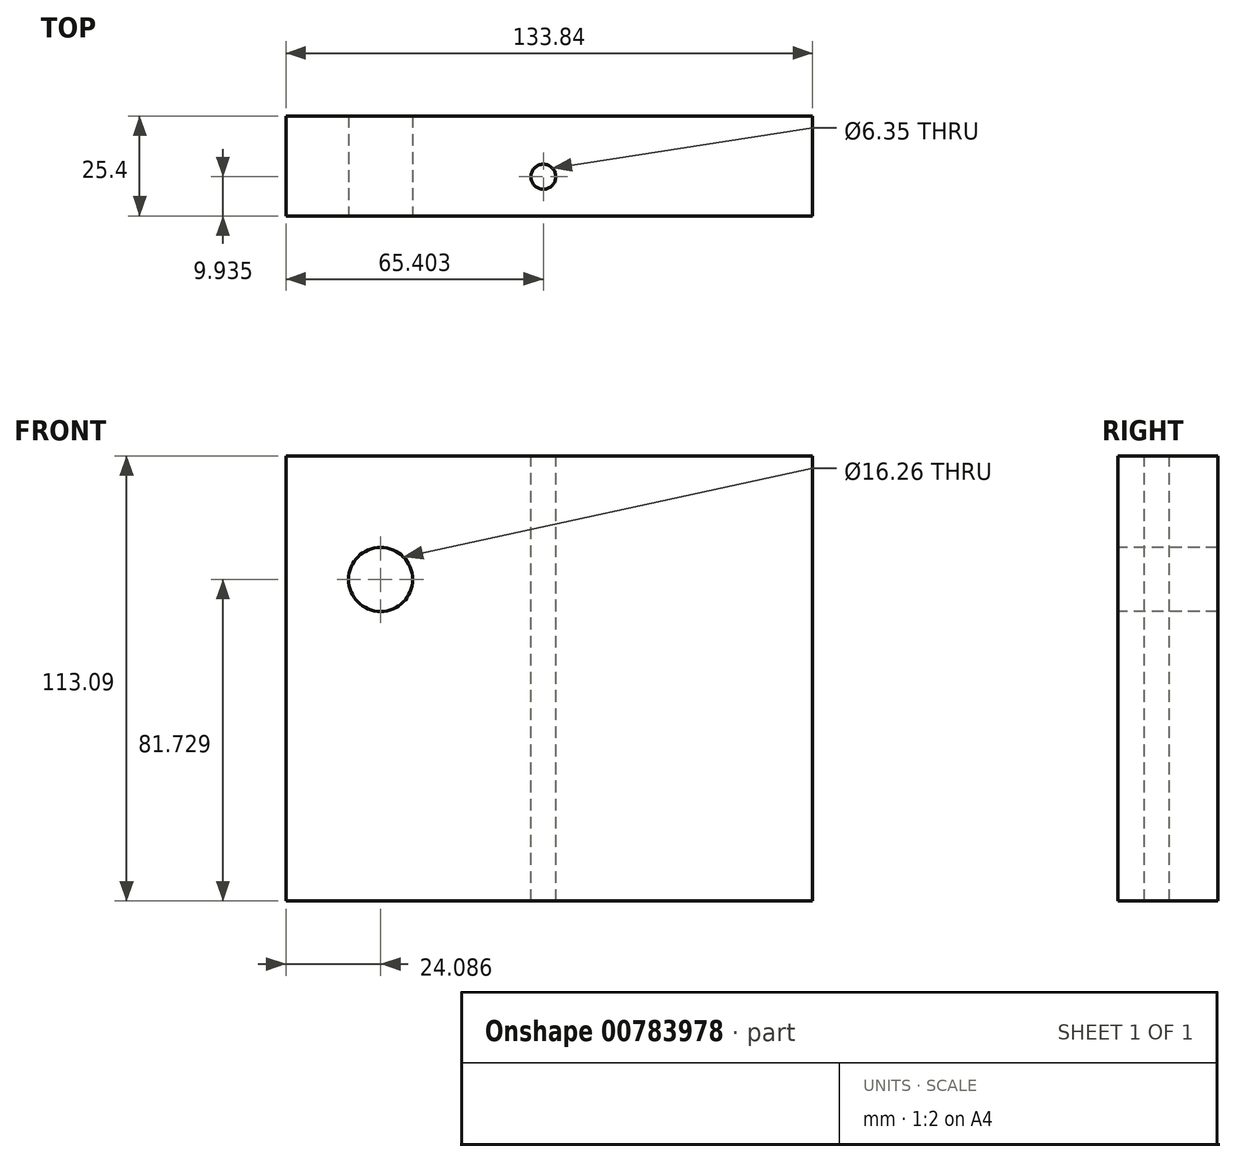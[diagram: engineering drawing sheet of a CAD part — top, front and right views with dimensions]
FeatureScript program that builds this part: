
annotation { "Feature Type Name" : "Feature", "Feature Type Description" : "" }
export const myFeature = defineFeature(function(context is Context, id is Id, definition is map)
    precondition{}
    {
        {
            var Q0;
            Q0=qCreatedBy(makeId("Front.planeOp"),FACE);
            var sketch = newSketch(context, id + "F0", { "sketchPlane" : qUnion([Q0])});
            skLineSegment(sketch, "E0.bottom", {"start": v(0, 0) * mm, "end": v(133.84, 0) * mm});
            skLineSegment(sketch, "E0.top", {"start": v(0, 113.09) * mm, "end": v(133.84, 113.09) * mm});
            skLineSegment(sketch, "E0.left", {"start": v(0, 0) * mm, "end": v(0, 113.09) * mm});
            skLineSegment(sketch, "E0.right", {"start": v(133.84, 0) * mm, "end": v(133.84, 113.09) * mm});
            skSolve(sketch);
        }
        {
            var Q0;
            Q0=makeQuery(id+"F0.imprint","IMPRINT",FACE,{"disambiguationData":[TD([[makeQuery(id+"F0.imprint","IMPRINT",EDGE,{"derivedFrom":sQuery(id+"F0.wireOp",EDGE,"E0.bottom")}),1.0]])]});
            extrude(context, id + "F1", {"entities" : qUnion([Q0]), "depth" : 25.4 * mm, "offsetDistance" : 25.4 * mm});
        }
        {
            var Q0;
            Q0=makeQuery(id+"F1.opExtrude","CAP_FACE",FACE,{"disambiguationData":[OSD([sQuery(id+"F0.wireOp",EDGE,"E0.bottom"),sQuery(id+"F0.wireOp",EDGE,"E0.top"),sQuery(id+"F0.wireOp",EDGE,"E0.left"),sQuery(id+"F0.wireOp",EDGE,"E0.right")])],"isStart":false});
            var sketch = newSketch(context, id + "F2", { "sketchPlane" : qUnion([Q0])});
            skCircle(sketch, "E1", {"center": v(24.09, 81.73) * mm, "radius": 8.13 * mm});
            skSolve(sketch);
        }
        {
            var Q0;
            Q0=makeQuery(id+"F2.imprint","IMPRINT",FACE,{"disambiguationData":[TD([[makeQuery(id+"F2.imprint","IMPRINT",EDGE,{"derivedFrom":sQuery(id+"F2.wireOp",EDGE,"E1")}),1.0]])]});
            extrude(context, id + "F3", {"entities" : qUnion([Q0]), "operationType" : NewBodyOperationType.REMOVE, "oppositeDirection" : true, "depth" : 25.4 * mm, "offsetDistance" : 25.4 * mm});
        }
        {
            var Q0;
            Q0=makeQuery(id+"F1.opExtrude","SWEPT_FACE",FACE,{"disambiguationData":[OSD([sQuery(id+"F0.wireOp",EDGE,"E0.top")])]});
            var sketch = newSketch(context, id + "F4", { "sketchPlane" : qUnion([Q0])});
            skCircle(sketch, "E2", {"center": v(65.4, -15.47) * mm, "radius": 9.93 * mm});
            skSolve(sketch);
        }
        {
            var Q0;
            Q0=sQuery(id+"F4.wireOp",VERTEX,"E2.center");
            var Q1;
            Q1=makeQuery(id+"F1.opExtrude","SWEPT_BODY",BODY,{"disambiguationData":[OSD([sQuery(id+"F0.wireOp",EDGE,"E0.bottom"),sQuery(id+"F0.wireOp",EDGE,"E0.top"),sQuery(id+"F0.wireOp",EDGE,"E0.left"),sQuery(id+"F0.wireOp",EDGE,"E0.right")])]});
            hole(context, id + "F5", {"style" : HoleStyle.SIMPLE, "endStyle" : HoleEndStyle.THROUGH, "holeDiameter" : 6.35 * mm, "majorDiameter" : 6.35 * mm, "isTappedThrough" : true, "tappedDepth" : 12.7 * mm, "tapClearance" : 3, "locations" : qUnion([Q0]), "scope" : qUnion([Q1])});
        }
    });
